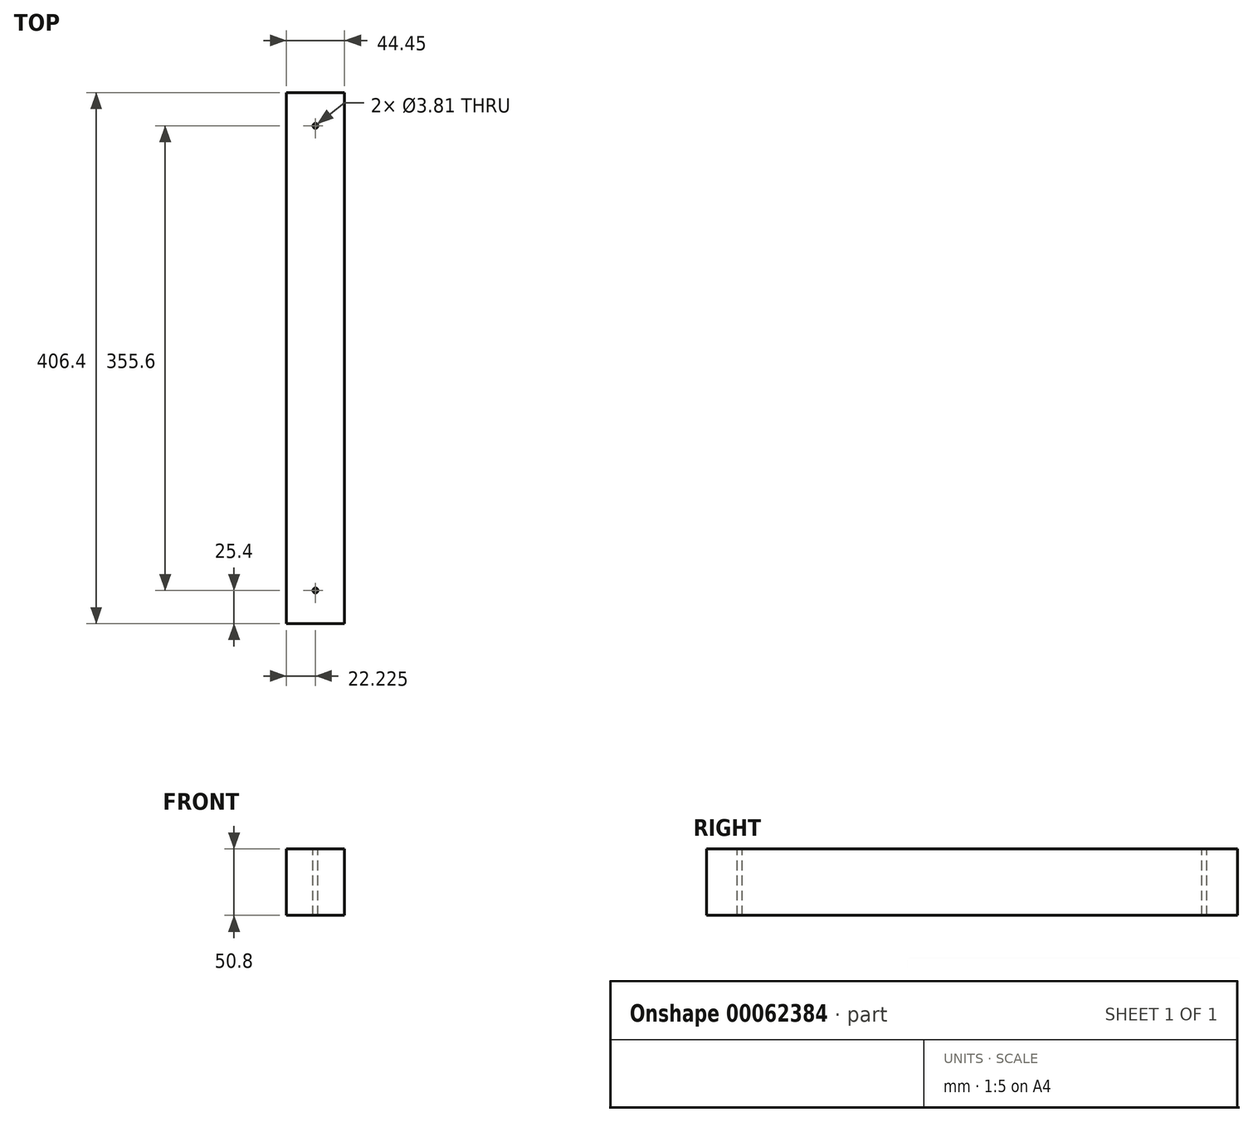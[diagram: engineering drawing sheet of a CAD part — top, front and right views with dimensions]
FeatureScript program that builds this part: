
annotation { "Feature Type Name" : "Feature", "Feature Type Description" : "" }
export const myFeature = defineFeature(function(context is Context, id is Id, definition is map)
    precondition{}
    {
        {
            var Q0;
            Q0=qCreatedBy(makeId("Top.planeOp"),FACE);
            var sketch = newSketch(context, id + "F0", { "sketchPlane" : qUnion([Q0])});
            skLineSegment(sketch, "E0.bottom", {"start": v(0, 0) * mm, "end": v(44.45, 0) * mm});
            skLineSegment(sketch, "E0.top", {"start": v(0, 406.4) * mm, "end": v(44.45, 406.4) * mm});
            skLineSegment(sketch, "E0.left", {"start": v(0, 0) * mm, "end": v(0, 406.4) * mm});
            skLineSegment(sketch, "E0.right", {"start": v(44.45, 0) * mm, "end": v(44.45, 406.4) * mm});
            skSolve(sketch);
        }
        {
            var Q0;
            Q0=makeQuery(id+"F0.imprint","IMPRINT",FACE,{"disambiguationData":[TD([[makeQuery(id+"F0.imprint","IMPRINT",EDGE,{"derivedFrom":sQuery(id+"F0.wireOp",EDGE,"E0.bottom")}),1.0]])]});
            extrude(context, id + "F1", {"entities" : qUnion([Q0]), "depth" : 50.8 * mm});
        }
        {
            var Q0;
            Q0=makeQuery(id+"F1.opExtrude","CAP_FACE",FACE,{"disambiguationData":[OSD([sQuery(id+"F0.wireOp",EDGE,"E0.bottom"),sQuery(id+"F0.wireOp",EDGE,"E0.top"),sQuery(id+"F0.wireOp",EDGE,"E0.left"),sQuery(id+"F0.wireOp",EDGE,"E0.right")])],"isStart":false});
            var sketch = newSketch(context, id + "F2", { "sketchPlane" : qUnion([Q0])});
            skCircle(sketch, "E1", {"center": v(22.22, 381) * mm, "radius": 1.9 * mm});
            skPoint(sketch, "E1.centerSnap0", {"position": v(22.22, 406.4) * mm});
            skCircle(sketch, "E2", {"center": v(22.22, 25.4) * mm, "radius": 1.9 * mm});
            skSolve(sketch);
        }
        {
            var Q0;
            Q0=qSketchRegion(id+"F2",true);
            extrude(context, id + "F3", {"entities" : qUnion([Q0]), "operationType" : NewBodyOperationType.REMOVE, "endBound" : BoundingType.UP_TO_NEXT, "oppositeDirection" : true, "depth" : 25.4 * mm});
        }
    });
